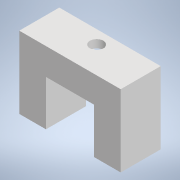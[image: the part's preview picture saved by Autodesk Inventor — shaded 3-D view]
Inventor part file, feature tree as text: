
AUTODESK INVENTOR PART (.ipt)
format: ipt  version: 2022 (Build 260153000, 153)  size: 131,072 bytes
history: native  units: mm
features: sketch x2, extrude x2, hole x1
ambient origin geometry x8: Origin, YZ Plane, XZ Plane, XY Plane, X Axis, Y Axis, Z Axis, Center Point
bodies: Solid1 (feature_tree)
feature tree (5):
  sketch  "Sketch1"  dims[d0=0.5mm d1=0.5mm]
  extrude  "Extrusion1"  Depth=0.5mm
  extrude  "Extrusion2"  Depth=4.0mm
  hole  "Hole1"  [1 undecoded]
  sketch  "Sketch2"  dims[d2=0.5mm d3=0.5mm d4=0.5mm d5=3.0mm d6=10.0mm d7=0.0mm d8=5.0mm d9=0.0mm d10=5.0mm d11=9.0mm d12=10.0mm d13=5.0mm d14=6.0mm d15=4.0mm d16=2.0mm d17=90.0deg d18=300.0mm d19=20.594885mm]
note: 1 required parameter value undecoded (feature->parameter linkage not recoverable at this tier; creation-order binding heuristic only, values carry confidence <= 0.55)
